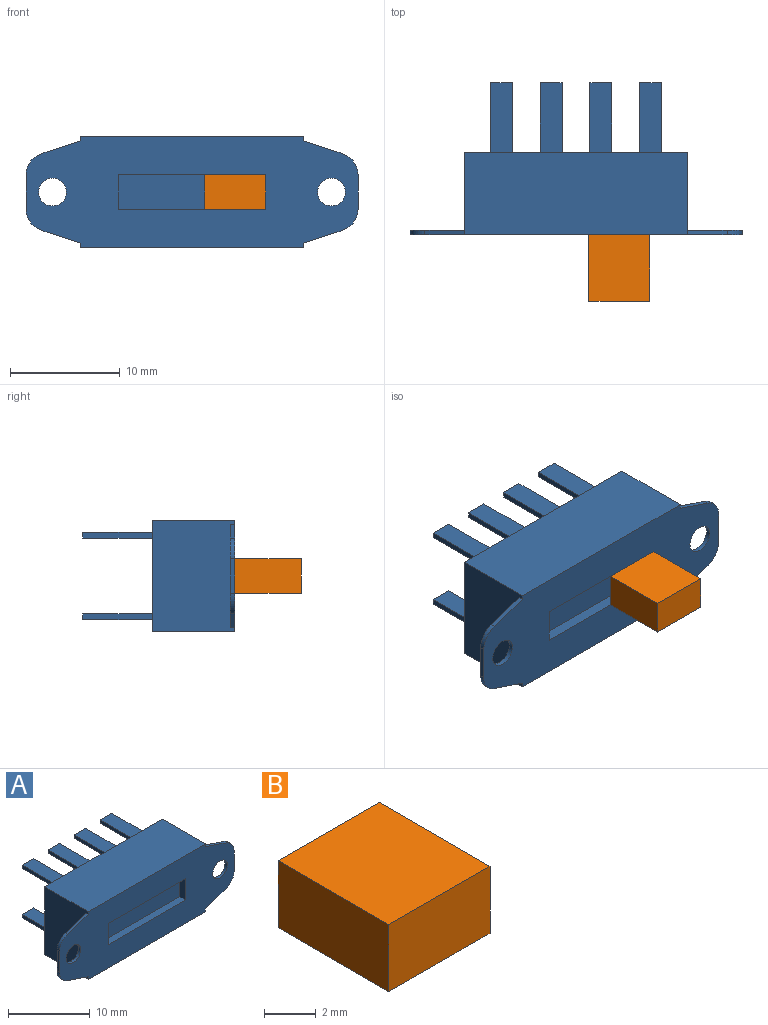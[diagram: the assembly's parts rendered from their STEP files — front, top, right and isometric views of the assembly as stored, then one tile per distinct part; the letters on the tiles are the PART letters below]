
ASSEMBLY  parts=2 mates=1
PART A: 65 faces, bbox 30.2x13.8x10.2 mm
  f0: plane 30.23x10.16mm, normal (0,-1,0), area 228.1mm2, adj f4,f5,f6,f7,f8,f9,f10,f11
  f1: plane 20.32x10.16mm, normal (0,1,0), area 198.4mm2, adj f4,f10,f11,f18,f20,f21,f22,f23
  f2: plane 9.34x4.96mm, normal (0,1,0), area 32.2mm2, adj f5,f6,f7,f8,f9,f10,f19
  f3: plane 9.34x4.96mm, normal (0,1,0), area 32.2mm2, adj f12,f13,f14,f15,f16,f17,f18
  f4: plane 20.32x7.49mm, normal (0,0,-1), area 152.2mm2, adj f0,f1,f10,f18
  f5: plane 3.59x1.21mm, normal (0.32,0,-0.95), area 1.6mm2, adj f0,f2,f6,f10
  f6: cylinder r=2mm len=1.9mm, axis (0,1,0), area 1mm2, adj f0,f2,f5,f7
  f7: plane 3.13x0.41mm, normal (1,0,0), area 1.3mm2, adj f0,f2,f6,f8
  f8: cylinder r=2mm len=1.9mm, axis (0,1,0), area 1mm2, adj f0,f2,f7,f9
  f9: plane 3.59x1.21mm, normal (0.32,0,0.95), area 1.6mm2, adj f0,f2,f8,f10
  f10: plane 10.16x7.49mm, normal (1,0,0), area 72.3mm2, adj f0,f1,f2,f4,f5,f9,f11
  f11: plane 20.32x7.49mm, normal (0,0,1), area 152.2mm2, adj f0,f1,f10,f18
  f12: plane 3.59x1.21mm, normal (-0.32,0,0.95), area 1.6mm2, adj f0,f3,f13,f18
  f13: cylinder r=2mm len=1.9mm, axis (0,1,0), area 1mm2, adj f0,f3,f12,f14
  f14: plane 3.13x0.41mm, normal (-1,0,0), area 1.3mm2, adj f0,f3,f13,f15
  f15: cylinder r=2mm len=1.9mm, axis (0,1,0), area 1mm2, adj f0,f3,f14,f16
  f16: plane 3.59x1.21mm, normal (-0.32,0,-0.95), area 1.6mm2, adj f0,f3,f15,f18
  f17: cylinder r=1.27mm len=2.54mm, axis (0,1,0), area 3.3mm2, adj f0,f3
  f18: plane 10.16x7.49mm, normal (-1,0,0), area 72.3mm2, adj f0,f1,f3,f4,f11,f12,f16
  f19: cylinder r=1.27mm len=2.54mm, axis (0,1,0), area 3.3mm2, adj f0,f2
  f20: plane 6.35x0.51mm, normal (1,0,0), area 3.2mm2, adj f1,f21,f23,f24
  f21: plane 6.35x1.98mm, normal (0,0,-1), area 12.6mm2, adj f1,f20,f22,f24
  f22: plane 6.35x0.51mm, normal (-1,0,0), area 3.2mm2, adj f1,f21,f23,f24
  f23: plane 6.35x1.98mm, normal (0,0,1), area 12.6mm2, adj f1,f20,f22,f24
  f24: plane 1.98x0.51mm, normal (0,1,0), area 1mm2, adj f20,f21,f22,f23
  f25: plane 6.35x1.98mm, normal (0,0,1), area 12.6mm2, adj f1,f26,f28,f29
  f26: plane 6.35x0.51mm, normal (1,0,0), area 3.2mm2, adj f1,f25,f27,f29
  f27: plane 6.35x1.98mm, normal (0,0,-1), area 12.6mm2, adj f1,f26,f28,f29
  f28: plane 6.35x0.51mm, normal (-1,0,0), area 3.2mm2, adj f1,f25,f27,f29
  f29: plane 1.98x0.51mm, normal (0,1,0), area 1mm2, adj f25,f26,f27,f28
  f30: plane 6.35x1.98mm, normal (0,0,1), area 12.6mm2, adj f1,f31,f33,f34
  f31: plane 6.35x0.51mm, normal (1,0,0), area 3.2mm2, adj f1,f30,f32,f34
  f32: plane 6.35x1.98mm, normal (0,0,-1), area 12.6mm2, adj f1,f31,f33,f34
  f33: plane 6.35x0.51mm, normal (-1,0,0), area 3.2mm2, adj f1,f30,f32,f34
  f34: plane 1.98x0.51mm, normal (0,1,0), area 1mm2, adj f30,f31,f32,f33
  f35: plane 6.35x1.98mm, normal (0,0,1), area 12.6mm2, adj f1,f36,f38,f39
  f36: plane 6.35x0.51mm, normal (1,0,0), area 3.2mm2, adj f1,f35,f37,f39
  f37: plane 6.35x1.98mm, normal (0,0,-1), area 12.6mm2, adj f1,f36,f38,f39
  f38: plane 6.35x0.51mm, normal (-1,0,0), area 3.2mm2, adj f1,f35,f37,f39
  f39: plane 1.98x0.51mm, normal (0,1,0), area 1mm2, adj f35,f36,f37,f38
  f40: plane 6.35x1.98mm, normal (0,0,1), area 12.6mm2, adj f1,f41,f43,f44
  f41: plane 6.35x0.51mm, normal (1,0,0), area 3.2mm2, adj f1,f40,f42,f44
  f42: plane 6.35x1.98mm, normal (0,0,-1), area 12.6mm2, adj f1,f41,f43,f44
  f43: plane 6.35x0.51mm, normal (-1,0,0), area 3.2mm2, adj f1,f40,f42,f44
  f44: plane 1.98x0.51mm, normal (0,1,0), area 1mm2, adj f40,f41,f42,f43
  f45: plane 6.35x1.98mm, normal (0,0,1), area 12.6mm2, adj f1,f46,f48,f49
  f46: plane 6.35x0.51mm, normal (1,0,0), area 3.2mm2, adj f1,f45,f47,f49
  f47: plane 6.35x1.98mm, normal (0,0,-1), area 12.6mm2, adj f1,f46,f48,f49
  f48: plane 6.35x0.51mm, normal (-1,0,0), area 3.2mm2, adj f1,f45,f47,f49
  f49: plane 1.98x0.51mm, normal (0,1,0), area 1mm2, adj f45,f46,f47,f48
  f50: plane 6.35x1.98mm, normal (0,0,1), area 12.6mm2, adj f1,f51,f53,f54
  f51: plane 6.35x0.51mm, normal (1,0,0), area 3.2mm2, adj f1,f50,f52,f54
  f52: plane 6.35x1.98mm, normal (0,0,-1), area 12.6mm2, adj f1,f51,f53,f54
  f53: plane 6.35x0.51mm, normal (-1,0,0), area 3.2mm2, adj f1,f50,f52,f54
  f54: plane 1.98x0.51mm, normal (0,1,0), area 1mm2, adj f50,f51,f52,f53
  f55: plane 6.35x1.98mm, normal (0,0,1), area 12.6mm2, adj f1,f56,f58,f59
  f56: plane 6.35x0.51mm, normal (1,0,0), area 3.2mm2, adj f1,f55,f57,f59
  f57: plane 6.35x1.98mm, normal (0,0,-1), area 12.6mm2, adj f1,f56,f58,f59
  f58: plane 6.35x0.51mm, normal (-1,0,0), area 3.2mm2, adj f1,f55,f57,f59
  f59: plane 1.98x0.51mm, normal (0,1,0), area 1mm2, adj f55,f56,f57,f58
  f60: plane 3.18x1mm, normal (-1,0,0), area 3.2mm2, adj f0,f61,f63,f64
  f61: plane 13.42x1mm, normal (0,0,-1), area 13.4mm2, adj f0,f60,f62,f64
  f62: plane 3.18x1mm, normal (1,0,0), area 3.2mm2, adj f0,f61,f63,f64
  f63: plane 13.42x1mm, normal (0,0,1), area 13.4mm2, adj f0,f60,f62,f64
  f64: plane 13.42x3.18mm, normal (0,-1,0), area 42.7mm2, adj f60,f61,f62,f63
PART B: 6 faces, bbox 5.5x6.1x3.2 mm
  f0: plane 6.08x3.18mm, normal (1,0,0), area 19.3mm2, adj f1,f3,f4,f5
  f1: plane 6.08x5.54mm, normal (0,0,1), area 33.7mm2, adj f0,f2,f4,f5
  f2: plane 6.08x3.18mm, normal (-1,0,0), area 19.3mm2, adj f1,f3,f4,f5
  f3: plane 6.08x5.54mm, normal (0,0,-1), area 33.7mm2, adj f0,f2,f4,f5
  f4: plane 5.54x3.18mm, normal (0,-1,0), area 17.6mm2, adj f0,f1,f2,f3
  f5: plane 5.54x3.18mm, normal (0,1,0), area 17.6mm2, adj f0,f1,f2,f3
PLACE A t=(1.47,3.28,1.93)mm
PLACE B t=(1.47,2.28,1.93)mm
MATE pin_slot B.f5 <-> A.f0  axis (0,1,0) through (5.41,2.87,1.93)mm
